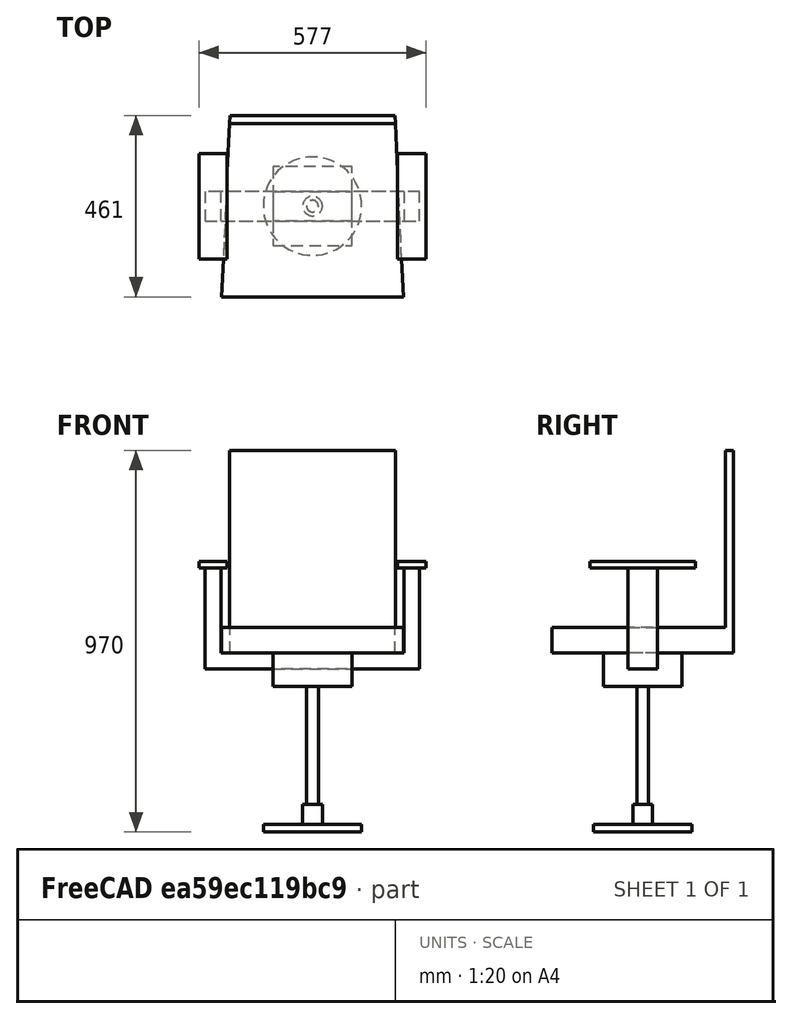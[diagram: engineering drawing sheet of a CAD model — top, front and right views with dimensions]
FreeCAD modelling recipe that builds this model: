
FCSTD DOCUMENT  (FreeCAD 1.0R39109 (Git))
Label: chair02_005
License: All rights reserved
LicenseURL: https://en.wikipedia.org/wiki/All_rights_reserved
objects: TechDraw::DrawViewDimension×26, Sketcher::SketchObject×10, PartDesign::Pad×10, TechDraw::DrawViewAnnotation×9, PartDesign::Body×5, PartDesign::ShapeBinder×4, TechDraw::DrawSVGTemplate×3, TechDraw::DrawProjGroupItem×3, TechDraw::DrawPage×3, TechDraw::DrawViewSection×3, App::Part×1
note: 108 computed .brp shape members not serialized (recipe doc carries the construction recipe); baked Part::Feature solids carry a one-line shape summary decoded from their .brp

FEATURE [Sketcher::SketchObject] Sketch
  ArcFitTolerance = 1e-06
  AttachmentSupport = -> [XY_Plane]
  FullyConstrained = true
  MakeInternals = false
  MapMode = 5
  sketch-geometry (1):
    g0: Circle CenterX=0 CenterY=0 CenterZ=0 NormalX=0 NormalY=0 NormalZ=1 AngleXU=0 Radius=125
  constraints (2):
    c: Diameter(g0) = 250
    c: Coincident(g0,g-1)
FEATURE [PartDesign::Pad] Pad
  Direction = (0,0,1)
  Length = 20
  Length2 = 10
  Profile = -> Sketch
  ReferenceAxis = -> Sketch [N_Axis]
  Refine = true
  Suppressed = false
  Type = 0
FEATURE [Sketcher::SketchObject] Sketch001
  ArcFitTolerance = 1e-06
  AttachmentSupport = -> [Pad]
  FullyConstrained = true
  MakeInternals = false
  MapMode = 5
  Placement = pos=(0,0,20) rot=(0,0,1;0rad)
  sketch-geometry (1):
    g0: Circle CenterX=0 CenterY=0 CenterZ=0 NormalX=0 NormalY=0 NormalZ=1 AngleXU=0 Radius=25
  constraints (2):
    c: Diameter(g0) = 50
    c: Coincident(g0,g-1)
FEATURE [PartDesign::Pad] Pad001
  BaseFeature = -> Pad
  Direction = (0,0,1)
  Length = 50
  Length2 = 10
  Profile = -> Sketch001
  ReferenceAxis = -> Sketch001 [N_Axis]
  Refine = true
  Suppressed = false
  Type = 0
FEATURE [PartDesign::Body] Body  label="Body1"
  AllowCompound = false
  Group = -> [Sketch,Pad,Sketch001,Pad001]
  Origin = -> Origin
  Tip = -> Pad001
FEATURE [PartDesign::ShapeBinder] CopyPad001  label="Body2_Sketch_P.lane"
  Placement = pos=(0,0,50) rot=(0,0,1;0rad)
  TraceSupport = false
FEATURE [Sketcher::SketchObject] Sketch002
  ArcFitTolerance = 1e-06
  AttachmentSupport = -> [CopyPad001]
  FullyConstrained = true
  MakeInternals = false
  MapMode = 5
  Placement = pos=(0,0,70) rot=(0,0,1;0rad)
  sketch-geometry (1):
    g0: Circle CenterX=0 CenterY=0 CenterZ=0 NormalX=0 NormalY=0 NormalZ=1 AngleXU=0 Radius=15
  constraints (2):
    c: Diameter(g0) = 30
    c: Coincident(g0,g-1)
FEATURE [PartDesign::Pad] Pad002
  Direction = (0,0,1)
  Length = 300
  Length2 = 10
  Placement = pos=(0,0,50) rot=(0,0,1;0rad)
  Profile = -> Sketch002
  ReferenceAxis = -> Sketch002 [N_Axis]
  Refine = true
  Suppressed = false
  Type = 0
FEATURE [PartDesign::Body] Body001  label="Body2"
  AllowCompound = false
  Group = -> [CopyPad001,Sketch002,Pad002]
  Origin = -> Origin001
  Tip = -> Pad002
FEATURE [PartDesign::ShapeBinder] CopyPad002  label="Body3_Sketch_Plane"
  Placement = pos=(0,0,300) rot=(0,0,1;0rad)
  TraceSupport = false
FEATURE [Sketcher::SketchObject] Sketch003
  ArcFitTolerance = 1e-06
  AttachmentSupport = -> [CopyPad002]
  FullyConstrained = true
  MakeInternals = false
  MapMode = 5
  Placement = pos=(0,0,370) rot=(0,0,1;0rad)
  sketch-geometry (5):
    g0: LineSegment StartX=-100 StartY=-100 StartZ=0 EndX=100 EndY=-100 EndZ=0
    g1: LineSegment StartX=100 StartY=-100 StartZ=0 EndX=100 EndY=100 EndZ=0
    g2: LineSegment StartX=100 StartY=100 StartZ=0 EndX=-100 EndY=100 EndZ=0
    g3: LineSegment StartX=-100 StartY=100 StartZ=0 EndX=-100 EndY=-100 EndZ=0
    g4: GeomPoint [constr] X=0 Y=0 Z=0
  constraints (12):
    c: Coincident(g0,g1)
    c: Coincident(g1,g2)
    c: Coincident(g2,g3)
    c: Coincident(g3,g0)
    c: Horizontal(g0)
    c: Horizontal(g2)
    c: Vertical(g1)
    c: Vertical(g3)
    c: Symmetric(g2,g0,g4)
    c: Distance(g1,g3) = 200
    c: Distance(g0,g2) = 200
    c: Coincident(g4,g-1)
FEATURE [PartDesign::Pad] Pad003
  Direction = (0,0,1)
  Length = 45
  Length2 = 10
  Placement = pos=(0,0,300) rot=(0,0,1;0rad)
  Profile = -> Sketch003
  ReferenceAxis = -> Sketch003 [N_Axis]
  Refine = true
  Suppressed = false
  Type = 0
FEATURE [PartDesign::ShapeBinder] CopyPad003  label="Body4_Sketch_Plane"
  Placement = pos=(0,0,45) rot=(0,0,1;0rad)
  TraceSupport = false
FEATURE [Sketcher::SketchObject] Sketch004
  ArcFitTolerance = 1e-06
  AttachmentSupport = -> [CopyPad003]
  FullyConstrained = true
  MakeInternals = false
  MapMode = 5
  Placement = pos=(0,0,415) rot=(0,0,1;0rad)
  sketch-geometry (5):
    g0: LineSegment StartX=-272.5 StartY=-37.5 StartZ=0 EndX=272.5 EndY=-37.5 EndZ=0
    g1: LineSegment StartX=272.5 StartY=-37.5 StartZ=0 EndX=272.5 EndY=37.5 EndZ=0
    g2: LineSegment StartX=272.5 StartY=37.5 StartZ=0 EndX=-272.5 EndY=37.5 EndZ=0
    g3: LineSegment StartX=-272.5 StartY=37.5 StartZ=0 EndX=-272.5 EndY=-37.5 EndZ=0
    g4: GeomPoint [constr] X=0 Y=0 Z=0
  constraints (12):
    c: Coincident(g0,g1)
    c: Coincident(g1,g2)
    c: Coincident(g2,g3)
    c: Coincident(g3,g0)
    c: Horizontal(g0)
    c: Horizontal(g2)
    c: Vertical(g1)
    c: Vertical(g3)
    c: Symmetric(g2,g0,g4)
    c: Distance(g1,g3) = 545
    c: Distance(g0,g2) = 75
    c: Coincident(g4,g-1)
FEATURE [PartDesign::Pad] Pad004
  Direction = (0,0,1)
  Length = 40
  Length2 = 10
  Placement = pos=(0,0,45) rot=(0,0,1;0rad)
  Profile = -> Sketch004
  ReferenceAxis = -> Sketch004 [N_Axis]
  Refine = true
  Suppressed = false
  Type = 0
FEATURE [Sketcher::SketchObject] Sketch005
  ArcFitTolerance = 1e-06
  AttachmentSupport = -> [Pad004]
  ExternalGeometry = -> [Pad004]
  FullyConstrained = true
  MakeInternals = false
  MapMode = 5
  Placement = pos=(0,0,455) rot=(0,0,1;0rad)
  sketch-geometry (8):
    g0: LineSegment StartX=-272.5 StartY=37.5 StartZ=0 EndX=-272.5 EndY=-37.5 EndZ=0
    g1: LineSegment StartX=-272.5 StartY=-37.5 StartZ=0 EndX=-232.5 EndY=-37.5 EndZ=0
    g2: LineSegment StartX=-232.5 StartY=-37.5 StartZ=0 EndX=-232.5 EndY=37.5 EndZ=0
    g3: LineSegment StartX=-232.5 StartY=37.5 StartZ=0 EndX=-272.5 EndY=37.5 EndZ=0
    g4: LineSegment StartX=272.5 StartY=37.5 StartZ=0 EndX=232.5 EndY=37.5 EndZ=0
    g5: LineSegment StartX=232.5 StartY=37.5 StartZ=0 EndX=232.5 EndY=-37.5 EndZ=0
    g6: LineSegment StartX=232.5 StartY=-37.5 StartZ=0 EndX=272.5 EndY=-37.5 EndZ=0
    g7: LineSegment StartX=272.5 StartY=-37.5 StartZ=0 EndX=272.5 EndY=37.5 EndZ=0
  constraints (22):
    c: Coincident(g0,g1)
    c: Coincident(g1,g2)
    c: Coincident(g2,g3)
    c: Coincident(g3,g0)
    c: Vertical(g0)
    c: Vertical(g2)
    c: Horizontal(g1)
    c: Horizontal(g3)
    c: Coincident(g0,g-3)
    c: PointOnObject(g1,g-4)
    c: DistanceX(g3,g3) = 40
    c: Coincident(g4,g5)
    c: Coincident(g5,g6)
    c: Coincident(g6,g7)
    c: Coincident(g7,g4)
    c: Horizontal(g4)
    c: Horizontal(g6)
    c: Vertical(g5)
    c: Vertical(g7)
    c: Coincident(g4,g-3)
    c: PointOnObject(g5,g-4)
    c: Equal(g4,g3)
FEATURE [PartDesign::Pad] Pad005
  BaseFeature = -> Pad004
  Direction = (0,0,1)
  Length = 216
  Length2 = 10
  Placement = pos=(0,0,45) rot=(0,0,1;0rad)
  Profile = -> Sketch005
  ReferenceAxis = -> Sketch005 [N_Axis]
  Refine = true
  Suppressed = false
  Type = 0
FEATURE [Sketcher::SketchObject] Sketch006
  ArcFitTolerance = 1e-06
  AttachmentSupport = -> [Pad005]
  ExternalGeometry = -> [Pad005]
  FullyConstrained = true
  MakeInternals = false
  MapMode = 5
  Placement = pos=(0,0,671) rot=(0,0,1;0rad)
  sketch-geometry (16):
    g0: LineSegment StartX=-288.5 StartY=134 StartZ=0 EndX=-288.5 EndY=-134 EndZ=0
    g1: LineSegment StartX=-288.5 StartY=-134 StartZ=0 EndX=-216.5 EndY=-134 EndZ=0
    g2: LineSegment StartX=-216.5 StartY=-134 StartZ=0 EndX=-216.5 EndY=134 EndZ=0
    g3: LineSegment StartX=-216.5 StartY=134 StartZ=0 EndX=-288.5 EndY=134 EndZ=0
    g4: LineSegment StartX=216.5 StartY=134 StartZ=0 EndX=216.5 EndY=-134 EndZ=0
    g5: LineSegment StartX=216.5 StartY=-134 StartZ=0 EndX=288.5 EndY=-134 EndZ=0
    g6: LineSegment StartX=288.5 StartY=-134 StartZ=0 EndX=288.5 EndY=134 EndZ=0
    g7: LineSegment StartX=288.5 StartY=134 StartZ=0 EndX=216.5 EndY=134 EndZ=0
    g8: LineSegment [constr] StartX=-272.5 StartY=37.5 StartZ=0 EndX=-232.5 EndY=-37.5 EndZ=0
    g9: LineSegment [constr] StartX=-252.5 StartY=0 StartZ=0 EndX=-272.5 EndY=-37.5 EndZ=0
    g10: LineSegment [constr] StartX=232.5 StartY=37.5 StartZ=0 EndX=272.5 EndY=-37.5 EndZ=0
    g11: LineSegment [constr] StartX=272.5 StartY=37.5 StartZ=0 EndX=252.5 EndY=0 EndZ=0
    g12: LineSegment [constr] StartX=-216.5 StartY=134 StartZ=0 EndX=-288.5 EndY=-134 EndZ=0
    g13: LineSegment [constr] StartX=-288.5 StartY=134 StartZ=0 EndX=-252.5 EndY=0 EndZ=0
    g14: LineSegment [constr] StartX=216.5 StartY=134 StartZ=0 EndX=288.5 EndY=-134 EndZ=0
    g15: LineSegment [constr] StartX=288.5 StartY=134 StartZ=0 EndX=252.5 EndY=0 EndZ=0
  constraints (38):
    c: Coincident(g0,g1)
    c: Coincident(g1,g2)
    c: Coincident(g2,g3)
    c: Coincident(g3,g0)
    c: Vertical(g0)
    c: Vertical(g2)
    c: Horizontal(g1)
    c: Horizontal(g3)
    c: Coincident(g4,g5)
    c: Coincident(g5,g6)
    c: Coincident(g6,g7)
    c: Coincident(g7,g4)
    c: Vertical(g4)
    c: Vertical(g6)
    c: Horizontal(g5)
    c: Horizontal(g7)
    c: Equal(g7,g3)
    c: Equal(g2,g4)
    c: DistanceX(g3,g3) = 72
    c: Coincident(g8,g-4)
    c: Coincident(g8,g-3)
    c: Coincident(g9,g-4)
    c: Coincident(g10,g-5)
    c: Coincident(g10,g-6)
    c: Coincident(g11,g-6)
    c: Symmetric(g10,g10,g11)
    c: Symmetric(g8,g8,g9)
    c: Coincident(g12,g2)
    c: Coincident(g12,g0)
    c: Coincident(g13,g0)
    c: Symmetric(g12,g12,g13)
    c: Coincident(g9,g13)
    c: Coincident(g14,g4)
    c: Coincident(g14,g5)
    c: Coincident(g15,g6)
    c: Symmetric(g14,g14,g15)
    c: Coincident(g15,g11)
    c: DistanceY(g2,g2) = 268
FEATURE [PartDesign::Pad] Pad006
  BaseFeature = -> Pad005
  Direction = (0,0,1)
  Length = 17
  Length2 = 10
  Placement = pos=(0,0,45) rot=(0,0,1;0rad)
  Profile = -> Sketch006
  ReferenceAxis = -> Sketch006 [N_Axis]
  Refine = true
  Suppressed = false
  Type = 0
FEATURE [PartDesign::Body] Body003  label="Body4"
  AllowCompound = false
  Group = -> [CopyPad003,Sketch004,Pad004,Sketch005,Pad005,Sketch006,Pad006]
  Origin = -> Origin003
  Tip = -> Pad006
FEATURE [PartDesign::ShapeBinder] CopyPad006  label="Body5_Sketch_Plane"
  Placement = pos=(0,0,45) rot=(0,0,1;0rad)
  TraceSupport = false
FEATURE [Sketcher::SketchObject] Sketch009
  ArcFitTolerance = 1e-06
  AttachmentSupport = -> [Pad003]
  ExternalGeometry = -> [Pad003]
  FullyConstrained = true
  MakeInternals = false
  MapMode = 5
  Placement = pos=(0,0,415) rot=(0,0,1;0rad)
  sketch-geometry (8):
    g0: LineSegment StartX=-100 StartY=100 StartZ=0 EndX=-100 EndY=37.5 EndZ=0
    g1: LineSegment StartX=-100 StartY=37.5 StartZ=0 EndX=100 EndY=37.5 EndZ=0
    g2: LineSegment StartX=100 StartY=37.5 StartZ=0 EndX=100 EndY=100 EndZ=0
    g3: LineSegment StartX=100 StartY=100 StartZ=0 EndX=-100 EndY=100 EndZ=0
    g4: LineSegment StartX=100 StartY=-100 StartZ=0 EndX=100 EndY=-37.5 EndZ=0
    g5: LineSegment StartX=100 StartY=-37.5 StartZ=0 EndX=-100 EndY=-37.5 EndZ=0
    g6: LineSegment StartX=-100 StartY=-37.5 StartZ=0 EndX=-100 EndY=-100 EndZ=0
    g7: LineSegment StartX=-100 StartY=-100 StartZ=0 EndX=100 EndY=-100 EndZ=0
  constraints (21):
    c: Coincident(g0,g1)
    c: Coincident(g1,g2)
    c: Coincident(g2,g3)
    c: Coincident(g3,g0)
    c: Vertical(g0)
    c: Vertical(g2)
    c: Horizontal(g1)
    c: Horizontal(g3)
    c: Coincident(g0,g-3)
    c: PointOnObject(g1,g-4)
    c: Coincident(g4,g5)
    c: Coincident(g5,g6)
    c: Coincident(g6,g7)
    c: Coincident(g7,g4)
    c: Vertical(g6)
    c: Horizontal(g5)
    c: Horizontal(g7)
    c: Coincident(g4,g-4)
    c: PointOnObject(g5,g-3)
    c: DistanceY(g4,g1) = 75
    c: Symmetric(g1,g4,g-1)
FEATURE [PartDesign::Pad] Pad009
  BaseFeature = -> Pad003
  Direction = (0,0,1)
  Length = 40
  Length2 = 10
  Placement = pos=(0,0,300) rot=(0,0,1;0rad)
  Profile = -> Sketch009
  ReferenceAxis = -> Sketch009 [N_Axis]
  Refine = true
  Suppressed = false
  Type = 0
FEATURE [PartDesign::Body] Body002  label="Body3"
  AllowCompound = false
  Group = -> [CopyPad002,Sketch003,Pad003,Sketch009,Pad009]
  Origin = -> Origin002
  Tip = -> Pad009
FEATURE [Sketcher::SketchObject] Sketch007
  ArcFitTolerance = 1e-06
  AttachmentSupport = -> [CopyPad006]
  FullyConstrained = true
  MakeInternals = false
  MapMode = 5
  Placement = pos=(0,0,455) rot=(0,0,1;0rad)
  sketch-geometry (8):
    g0: LineSegment StartX=-210 StartY=230.5 StartZ=0 EndX=-231 EndY=-230.5 EndZ=0
    g1: LineSegment StartX=-231 StartY=-230.5 StartZ=0 EndX=231 EndY=-230.5 EndZ=0
    g2: LineSegment StartX=231 StartY=-230.5 StartZ=0 EndX=210 EndY=230.5 EndZ=0
    g3: LineSegment StartX=210 StartY=230.5 StartZ=0 EndX=-210 EndY=230.5 EndZ=0
    g4: LineSegment [constr] StartX=210 StartY=230.5 StartZ=0 EndX=2.84e-14 EndY=0 EndZ=0
    g5: LineSegment [constr] StartX=2.84e-14 StartY=0 StartZ=0 EndX=-210 EndY=230.5 EndZ=0
    g6: LineSegment [constr] StartX=210 StartY=230.5 StartZ=0 EndX=210 EndY=0 EndZ=0
    g7: LineSegment [constr] StartX=231 StartY=-230.5 StartZ=0 EndX=231 EndY=0 EndZ=0
  constraints (20):
    c: Coincident(g2,g1)
    c: DistanceX(g1,g1) = 462
    c: DistanceX(g3,g3) = 420
    c: Coincident(g1,g0)
    c: Symmetric(g2,g0,g-2)
    c: Coincident(g2,g3)
    c: Coincident(g3,g0)
    c: Coincident(g4,g2)
    c: Coincident(g4,g-1)
    c: Coincident(g5,g4)
    c: Coincident(g5,g0)
    c: DistanceY(g2,g2) = 461
    c: Coincident(g6,g2)
    c: PointOnObject(g6,g-1)
    c: Vertical(g6)
    c: Coincident(g7,g1)
    c: PointOnObject(g7,g-1)
    c: Vertical(g7)
    c: Equal(g7,g6)
    c: Symmetric(g1,g0,g-2)
FEATURE [PartDesign::Pad] Pad007
  Direction = (0,0,1)
  Length = 65
  Length2 = 10
  Placement = pos=(0,0,45) rot=(0,0,1;0rad)
  Profile = -> Sketch007
  ReferenceAxis = -> Sketch007 [N_Axis]
  Refine = true
  Suppressed = false
  Type = 0
FEATURE [Sketcher::SketchObject] Sketch008
  ArcFitTolerance = 1e-06
  AttachmentSupport = -> [Pad007]
  ExternalGeometry = -> [Pad007]
  FullyConstrained = true
  MakeInternals = false
  MapMode = 5
  Placement = pos=(0,0,520) rot=(0,0,1;0rad)
  sketch-geometry (4):
    g0: LineSegment StartX=-210 StartY=230.5 StartZ=0 EndX=210 EndY=230.5 EndZ=0
    g1: LineSegment StartX=-210 StartY=230.5 StartZ=0 EndX=-210.957 EndY=209.5 EndZ=0
    g2: LineSegment StartX=-210.957 StartY=209.5 StartZ=0 EndX=210.957 EndY=209.5 EndZ=0
    g3: LineSegment StartX=210 StartY=230.5 StartZ=0 EndX=210.957 EndY=209.5 EndZ=0
  constraints (10):
    c: Coincident(g0,g-3)
    c: Coincident(g0,g-4)
    c: Coincident(g1,g0)
    c: PointOnObject(g1,g-3)
    c: Coincident(g2,g1)
    c: PointOnObject(g2,g-4)
    c: Horizontal(g2)
    c: Coincident(g3,g0)
    c: Coincident(g3,g2)
    c: DistanceY(g1,g1) = 21
FEATURE [PartDesign::Pad] Pad008
  BaseFeature = -> Pad007
  Direction = (0,0,1)
  Length = 450
  Length2 = 10
  Placement = pos=(0,0,45) rot=(0,0,1;0rad)
  Profile = -> Sketch008
  ReferenceAxis = -> Sketch008 [N_Axis]
  Refine = true
  Suppressed = false
  Type = 0
FEATURE [PartDesign::Body] Body004  label="Body5"
  AllowCompound = false
  Group = -> [CopyPad006,Sketch007,Pad007,Sketch008,Pad008]
  Origin = -> Origin004
  Tip = -> Pad008
FEATURE [App::Part] Part  label="chair02"
  Group = -> [Body,Body001,Body002,Body003,Body004]
  Origin = -> Origin005
FEATURE [TechDraw::DrawSVGTemplate] Template  label="テンプレート"
  Height = 210
  Orientation = 1
  Template = <userpath>/AppData/Local/Programs/FreeCAD 1.0/data/Mod/TechDraw/Templates/A4_Landscape_blank.svg
  Width = 297
FEATURE [TechDraw::DrawProjGroupItem] View
  CoarseView = false
  Direction = (0,0,1)
  Focus = 100
  HardHidden = true
  IsoCount = 0
  IsoHidden = false
  IsoVisible = false
  LockPosition = false
  Perspective = false
  Rotation = 0
  RotationVector = (1,0,0)
  Scale = 0.333333
  ScaleType = 2
  ScrubCount = 1
  SeamHidden = false
  SeamVisible = false
  SmoothHidden = false
  SmoothVisible = true
  Source = -> [Part]
  Type = 0
  X = 131.425
  XDirection = (1,0,0)
  Y = 107.897
FEATURE [TechDraw::DrawViewDimension] Dimension  label="寸法"
  AngleOverride = false
  Arbitrary = false
  ArbitraryTolerances = false
  BoxCorners = (2) [(-96.1666,-76.8333,0),(96.1666,76.8333,0)]
  EqualTolerance = true
  ExtensionAngle = 0
  FormatSpec = %.2w
  FormatSpecOverTolerance = %+.2w
  FormatSpecUnderTolerance = %+.2w
  Inverted = false
  LineAngle = 0
  LockPosition = false
  MeasureType = 1
  OverTolerance = 0
  References2D = -> [View]
  Rotation = 0
  Scale = 0.2
  ScaleType = 2
  TheoreticalExact = false
  Type = 1
  UnderTolerance = 0
  X = 0
  Y = 93.9298
FEATURE [TechDraw::DrawViewDimension] Dimension001  label="寸法001"
  AngleOverride = false
  Arbitrary = false
  ArbitraryTolerances = false
  BoxCorners = (2) [(-96.1666,-76.8333,0),(96.1666,76.8333,0)]
  EqualTolerance = true
  ExtensionAngle = 0
  FormatSpec = %.2w
  FormatSpecOverTolerance = %+.2w
  FormatSpecUnderTolerance = %+.2w
  Inverted = false
  LineAngle = 0
  LockPosition = false
  MeasureType = 1
  OverTolerance = 0
  References2D = -> [View]
  Rotation = 0
  Scale = 0.2
  ScaleType = 2
  TheoreticalExact = false
  Type = 2
  UnderTolerance = 0
  X = 135.701
  Y = 0
FEATURE [TechDraw::DrawViewDimension] Dimension002  label="寸法002"
  AngleOverride = false
  Arbitrary = false
  ArbitraryTolerances = false
  BoxCorners = (2) [(-96.1666,-76.8333,0),(96.1666,76.8333,0)]
  EqualTolerance = true
  ExtensionAngle = 0
  FormatSpec = %.2w
  FormatSpecOverTolerance = %+.2w
  FormatSpecUnderTolerance = %+.2w
  Inverted = false
  LineAngle = 0
  LockPosition = false
  MeasureType = 1
  OverTolerance = 0
  References2D = -> [View]
  Rotation = 0
  Scale = 0.2
  ScaleType = 2
  TheoreticalExact = false
  Type = 2
  UnderTolerance = 0
  X = 113.57
  Y = 61.6706
FEATURE [TechDraw::DrawViewDimension] Dimension003  label="寸法003"
  AngleOverride = false
  Arbitrary = false
  ArbitraryTolerances = false
  BoxCorners = (2) [(-96.1666,-76.8333,0),(96.1666,76.8333,0)]
  EqualTolerance = true
  ExtensionAngle = 0
  FormatSpec = %.2w
  FormatSpecOverTolerance = %+.2w
  FormatSpecUnderTolerance = %+.2w
  Inverted = false
  LineAngle = 0
  LockPosition = false
  MeasureType = 1
  OverTolerance = 0
  References2D = -> [View]
  Rotation = 0
  Scale = 0.2
  ScaleType = 2
  TheoreticalExact = false
  Type = 2
  UnderTolerance = 0
  X = 125.233
  Y = 0.063601
FEATURE [TechDraw::DrawViewDimension] Dimension004  label="寸法004"
  AngleOverride = false
  Arbitrary = false
  ArbitraryTolerances = false
  BoxCorners = (2) [(-96.1666,-76.8333,0),(96.1666,76.8333,0)]
  EqualTolerance = true
  ExtensionAngle = 0
  FormatSpec = %.2w
  FormatSpecOverTolerance = %+.2w
  FormatSpecUnderTolerance = %+.2w
  Inverted = false
  LineAngle = 0
  LockPosition = false
  MeasureType = 1
  OverTolerance = 0
  References2D = -> [View]
  Rotation = 0
  Scale = 0.2
  ScaleType = 2
  TheoreticalExact = false
  Type = 1
  UnderTolerance = 0
  X = -84.1666
  Y = 58.5053
FEATURE [TechDraw::DrawViewDimension] Dimension005  label="寸法005"
  AngleOverride = false
  Arbitrary = false
  ArbitraryTolerances = false
  BoxCorners = (2) [(-96.1666,-76.8333,0),(96.1666,76.8333,0)]
  EqualTolerance = true
  ExtensionAngle = 0
  FormatSpec = %.2w
  FormatSpecOverTolerance = %+.2w
  FormatSpecUnderTolerance = %+.2w
  Inverted = false
  LineAngle = 0
  LockPosition = false
  MeasureType = 1
  OverTolerance = 0
  References2D = -> [View]
  Rotation = 0
  Scale = 0.2
  ScaleType = 2
  TheoreticalExact = false
  Type = 2
  UnderTolerance = 0
  X = -108.801
  Y = 0
FEATURE [TechDraw::DrawViewDimension] Dimension006  label="寸法006"
  AngleOverride = false
  Arbitrary = false
  ArbitraryTolerances = false
  BoxCorners = (2) [(-96.1666,-76.8333,0),(96.1666,76.8333,0)]
  EqualTolerance = true
  ExtensionAngle = 0
  FormatSpec = %.2w
  FormatSpecOverTolerance = %+.2w
  FormatSpecUnderTolerance = %+.2w
  Inverted = false
  LineAngle = 0
  LockPosition = false
  MeasureType = 1
  OverTolerance = 0
  References2D = -> [View]
  Rotation = 0
  Scale = 0.2
  ScaleType = 2
  TheoreticalExact = false
  Type = 1
  UnderTolerance = 0
  X = 0
  Y = -83.8244
FEATURE [TechDraw::DrawPage] Page  label="用紙"
  KeepUpdated = true
  NextBalloonIndex = 1
  ProjectionType = 0
  Template = -> Template
  Views = -> [View,Dimension,Dimension001,Dimension002,Dimension003,Dimension004,Dimension005,Dimension006]
FEATURE [TechDraw::DrawSVGTemplate] Template001  label="テンプレート001"
  Height = 210
  Orientation = 1
  Template = <userpath>/AppData/Local/Programs/FreeCAD 1.0/data/Mod/TechDraw/Templates/A4_Landscape_blank.svg
  Width = 297
FEATURE [TechDraw::DrawSVGTemplate] Template002  label="テンプレート002"
  Height = 210
  Orientation = 1
  Template = <userpath>/AppData/Local/Programs/FreeCAD 1.0/data/Mod/TechDraw/Templates/A4_Landscape_blank.svg
  Width = 297
FEATURE [TechDraw::DrawProjGroupItem] View001
  CoarseView = false
  Direction = (0,-1,0)
  Focus = 100
  HardHidden = true
  IsoCount = 0
  IsoHidden = false
  IsoVisible = false
  LockPosition = false
  Perspective = false
  Rotation = 0
  RotationVector = (1,0,0)
  Scale = 0.2
  ScaleType = 2
  ScrubCount = 1
  SeamHidden = false
  SeamVisible = false
  SmoothHidden = false
  SmoothVisible = true
  Source = -> [Part]
  Type = 0
  X = 72.2264
  XDirection = (1,0,0)
  Y = 108.632
FEATURE [TechDraw::DrawViewSection] SectionView  label="セクション  - "
  BaseView = -> View001
  CoarseView = false
  CutSurfaceDisplay = 2
  Direction = (1e-16,0,1)
  FileGeomPattern = <userpath>\AppData\Local\Programs\FreeCAD 1.0\data\Mod/TechDraw/PAT/FCPAT.pat
  FileHatchPattern = <userpath>\AppData\Local\Programs\FreeCAD 1.0\data\Mod/TechDraw/Patterns/simple.svg
  Focus = 100
  FuseBeforeCut = false
  HardHidden = true
  HatchOffset = (0,0,0)
  HatchRotation = 0
  HatchScale = 1
  IsoCount = 0
  IsoHidden = false
  IsoVisible = false
  LockPosition = false
  NameGeomPattern = Diamond
  Perspective = false
  Rotation = 0
  Scale = 0.15
  ScaleType = 2
  ScrubCount = 1
  SeamHidden = false
  SeamVisible = false
  SectionDirection = 4
  SectionLineStretch = 1
  SectionNormal = (1e-16,0,1)
  SectionOrigin = (0,0,581)
  SmoothHidden = false
  SmoothVisible = true
  Source = -> [Part]
  TrimAfterCut = false
  UsePreviousCut = false
  X = 215.858
  XDirection = (1,0,-1e-16)
  Y = 166.085
FEATURE [TechDraw::DrawViewSection] SectionView001  label="セクション001  - "
  BaseView = -> View001
  CoarseView = false
  CutSurfaceDisplay = 2
  Direction = (1e-16,0,1)
  FileGeomPattern = <userpath>\AppData\Local\Programs\FreeCAD 1.0\data\Mod/TechDraw/PAT/FCPAT.pat
  FileHatchPattern = <userpath>\AppData\Local\Programs\FreeCAD 1.0\data\Mod/TechDraw/Patterns/simple.svg
  Focus = 100
  FuseBeforeCut = false
  HardHidden = true
  HatchOffset = (0,0,0)
  HatchRotation = 0
  HatchScale = 1
  IsoCount = 0
  IsoHidden = false
  IsoVisible = false
  LockPosition = false
  NameGeomPattern = Diamond
  Perspective = false
  Rotation = 0
  Scale = 0.15
  ScaleType = 2
  ScrubCount = 1
  SeamHidden = false
  SeamVisible = false
  SectionDirection = 4
  SectionLineStretch = 1
  SectionNormal = (1e-16,0,1)
  SectionOrigin = (0,0,437)
  SmoothHidden = false
  SmoothVisible = true
  Source = -> [Part]
  TrimAfterCut = false
  UsePreviousCut = false
  X = 215.086
  XDirection = (1,0,-1e-16)
  Y = 92.3168
FEATURE [TechDraw::DrawViewSection] SectionView002  label="セクション002  - "
  BaseView = -> View001
  CoarseView = false
  CutSurfaceDisplay = 2
  Direction = (1e-16,0,1)
  FileGeomPattern = <userpath>\AppData\Local\Programs\FreeCAD 1.0\data\Mod/TechDraw/PAT/FCPAT.pat
  FileHatchPattern = <userpath>\AppData\Local\Programs\FreeCAD 1.0\data\Mod/TechDraw/Patterns/simple.svg
  Focus = 100
  FuseBeforeCut = false
  HardHidden = true
  HatchOffset = (0,0,0)
  HatchRotation = 0
  HatchScale = 1
  IsoCount = 0
  IsoHidden = false
  IsoVisible = false
  LockPosition = false
  NameGeomPattern = Diamond
  Perspective = false
  Rotation = 0
  Scale = 0.15
  ScaleType = 2
  ScrubCount = 1
  SeamHidden = false
  SeamVisible = false
  SectionDirection = 4
  SectionLineStretch = 1
  SectionNormal = (1e-16,0,1)
  SectionOrigin = (0,0,200)
  SmoothHidden = false
  SmoothVisible = true
  Source = -> [Part]
  TrimAfterCut = false
  UsePreviousCut = false
  X = 214.868
  XDirection = (1,0,-1e-16)
  Y = 24.434
FEATURE [TechDraw::DrawViewDimension] Dimension007  label="寸法007"
  AngleOverride = false
  Arbitrary = false
  ArbitraryTolerances = false
  BoxCorners = (2) [(-40.875,-34.575,0),(40.875,34.575,0)]
  EqualTolerance = true
  ExtensionAngle = 0
  FormatSpec = %.2w
  FormatSpecOverTolerance = %+.2w
  FormatSpecUnderTolerance = %+.2w
  Inverted = false
  LineAngle = 0
  LockPosition = false
  MeasureType = 1
  OverTolerance = 0
  References2D = -> [SectionView]
  Rotation = 0
  Scale = 0.2
  ScaleType = 2
  TheoreticalExact = false
  Type = 1
  UnderTolerance = 0
  X = 48.3858
  Y = 24.3952
FEATURE [TechDraw::DrawViewDimension] Dimension008  label="寸法008"
  AngleOverride = false
  Arbitrary = false
  ArbitraryTolerances = false
  BoxCorners = (2) [(-40.875,-34.575,0),(40.875,34.575,0)]
  EqualTolerance = true
  ExtensionAngle = 0
  FormatSpec = %.2w
  FormatSpecOverTolerance = %+.2w
  FormatSpecUnderTolerance = %+.2w
  Inverted = false
  LineAngle = 0
  LockPosition = false
  MeasureType = 1
  OverTolerance = 0
  References2D = -> [SectionView]
  Rotation = 0
  Scale = 0.2
  ScaleType = 2
  TheoreticalExact = false
  Type = 2
  UnderTolerance = 0
  X = 59.3049
  Y = -11.5187
FEATURE [TechDraw::DrawViewDimension] Dimension009  label="寸法009"
  AngleOverride = false
  Arbitrary = false
  ArbitraryTolerances = false
  BoxCorners = (2) [(-40.875,-18.75,0),(40.875,18.75,0)]
  EqualTolerance = true
  ExtensionAngle = 0
  FormatSpec = %.2w
  FormatSpecOverTolerance = %+.2w
  FormatSpecUnderTolerance = %+.2w
  Inverted = false
  LineAngle = 0
  LockPosition = false
  MeasureType = 1
  OverTolerance = 0
  References2D = -> [SectionView001]
  Rotation = 0
  Scale = 0.2
  ScaleType = 2
  TheoreticalExact = false
  Type = 1
  UnderTolerance = 0
  X = 0
  Y = -24.3529
FEATURE [TechDraw::DrawViewDimension] Dimension010  label="寸法010"
  AngleOverride = false
  Arbitrary = false
  ArbitraryTolerances = false
  BoxCorners = (2) [(-40.875,-18.75,0),(40.875,18.75,0)]
  EqualTolerance = true
  ExtensionAngle = 0
  FormatSpec = %.2w
  FormatSpecOverTolerance = %+.2w
  FormatSpecUnderTolerance = %+.2w
  Inverted = false
  LineAngle = 0
  LockPosition = false
  MeasureType = 1
  OverTolerance = 0
  References2D = -> [SectionView001]
  Rotation = 0
  Scale = 0.2
  ScaleType = 2
  TheoreticalExact = false
  Type = 1
  UnderTolerance = 0
  X = -23.2227
  Y = -15.8558
FEATURE [TechDraw::DrawViewDimension] Dimension011  label="寸法011"
  AngleOverride = false
  Arbitrary = false
  ArbitraryTolerances = false
  BoxCorners = (2) [(-40.875,-18.75,0),(40.875,18.75,0)]
  EqualTolerance = true
  ExtensionAngle = 0
  FormatSpec = %.2w
  FormatSpecOverTolerance = %+.2w
  FormatSpecUnderTolerance = %+.2w
  Inverted = false
  LineAngle = 0
  LockPosition = false
  MeasureType = 1
  OverTolerance = 0
  References2D = -> [SectionView001]
  Rotation = 0
  Scale = 0.2
  ScaleType = 2
  TheoreticalExact = false
  Type = 2
  UnderTolerance = 0
  X = 58.5124
  Y = 0
FEATURE [TechDraw::DrawViewDimension] Dimension012  label="寸法012"
  AngleOverride = false
  Arbitrary = false
  ArbitraryTolerances = false
  BoxCorners = (2) [(-40.875,-18.75,0),(40.875,18.75,0)]
  EqualTolerance = true
  ExtensionAngle = 0
  FormatSpec = %.2w
  FormatSpecOverTolerance = %+.2w
  FormatSpecUnderTolerance = %+.2w
  Inverted = false
  LineAngle = 0
  LockPosition = false
  MeasureType = 1
  OverTolerance = 0
  References2D = -> [SectionView001]
  Rotation = 0
  Scale = 0.2
  ScaleType = 2
  TheoreticalExact = false
  Type = 2
  UnderTolerance = 0
  X = 72.3404
  Y = 0
FEATURE [TechDraw::DrawViewDimension] Dimension013  label="寸法013"
  AngleOverride = false
  Arbitrary = false
  ArbitraryTolerances = false
  BoxCorners = (2) [(-18.75,-18.75,0),(18.75,18.75,0)]
  EqualTolerance = true
  ExtensionAngle = 0
  FormatSpec = ⌀%.2w
  FormatSpecOverTolerance = %+.2w
  FormatSpecUnderTolerance = %+.2w
  Inverted = false
  LineAngle = 0
  LockPosition = false
  MeasureType = 1
  OverTolerance = 0
  References2D = -> [SectionView002]
  Rotation = 0
  Scale = 0.2
  ScaleType = 2
  TheoreticalExact = false
  Type = 5
  UnderTolerance = 0
  X = 8.10016
  Y = -8.95927
FEATURE [TechDraw::DrawViewDimension] Dimension014  label="寸法014"
  AngleOverride = false
  Arbitrary = false
  ArbitraryTolerances = false
  BoxCorners = (2) [(-18.75,-18.75,0),(18.75,18.75,0)]
  EqualTolerance = true
  ExtensionAngle = 0
  FormatSpec = ⌀%.2w
  FormatSpecOverTolerance = %+.2w
  FormatSpecUnderTolerance = %+.2w
  Inverted = false
  LineAngle = 0
  LockPosition = false
  MeasureType = 1
  OverTolerance = 0
  References2D = -> [SectionView002]
  Rotation = 0
  Scale = 0.2
  ScaleType = 2
  TheoreticalExact = false
  Type = 5
  UnderTolerance = 0
  X = 10.9229
  Y = 0.736379
FEATURE [TechDraw::DrawViewDimension] Dimension015  label="寸法015"
  AngleOverride = false
  Arbitrary = false
  ArbitraryTolerances = false
  BoxCorners = (2) [(-18.75,-18.75,0),(18.75,18.75,0)]
  EqualTolerance = true
  ExtensionAngle = 0
  FormatSpec = ⌀%.2w
  FormatSpecOverTolerance = %+.2w
  FormatSpecUnderTolerance = %+.2w
  Inverted = false
  LineAngle = 0
  LockPosition = false
  MeasureType = 1
  OverTolerance = 0
  References2D = -> [SectionView002]
  Rotation = 0
  Scale = 0.2
  ScaleType = 2
  TheoreticalExact = false
  Type = 5
  UnderTolerance = 0
  X = 22.705
  Y = 18.6549
FEATURE [TechDraw::DrawViewDimension] Dimension016  label="寸法016"
  AngleOverride = false
  Arbitrary = false
  ArbitraryTolerances = false
  BoxCorners = (2) [(-40.875,-34.575,0),(40.875,34.575,0)]
  EqualTolerance = true
  ExtensionAngle = 0
  FormatSpec = %.2w
  FormatSpecOverTolerance = %+.2w
  FormatSpecUnderTolerance = %+.2w
  Inverted = false
  LineAngle = 0
  LockPosition = false
  MeasureType = 1
  OverTolerance = 0
  References2D = -> [SectionView]
  Rotation = 0
  Scale = 0.2
  ScaleType = 2
  TheoreticalExact = false
  Type = 1
  UnderTolerance = 0
  X = 21.6748
  Y = -21.6209
FEATURE [TechDraw::DrawViewAnnotation] Annotation  label="注釈"
  Font = osifont
  LineSpace = 100
  LockPosition = false
  MaxWidth = -1
  Rotation = 0
  Scale = 0.2
  ScaleType = 2
  Text = A
  TextSize = 5
  TextStyle = 0
  X = 143.937
  Y = 118.99
FEATURE [TechDraw::DrawViewAnnotation] Annotation001  label="注釈001"
  Font = osifont
  LineSpace = 100
  LockPosition = false
  MaxWidth = -1
  Rotation = 0
  Scale = 0.2
  ScaleType = 2
  Text = A
  TextSize = 5
  TextStyle = 0
  X = 9.25009
  Y = 118.99
FEATURE [TechDraw::DrawViewAnnotation] Annotation002  label="注釈002"
  Font = osifont
  LineSpace = 100
  LockPosition = false
  MaxWidth = -1
  Rotation = 0
  Scale = 0.2
  ScaleType = 2
  Text = B
  TextSize = 5
  TextStyle = 0
  X = 9.25009
  Y = 89.4351
FEATURE [TechDraw::DrawViewAnnotation] Annotation003  label="注釈003"
  Font = osifont
  LineSpace = 100
  LockPosition = false
  MaxWidth = -1
  Rotation = 0
  Scale = 0.2
  ScaleType = 2
  Text = B
  TextSize = 5
  TextStyle = 0
  X = 145.458
  Y = 89.4351
FEATURE [TechDraw::DrawViewAnnotation] Annotation004  label="注釈004"
  Font = osifont
  LineSpace = 100
  LockPosition = false
  MaxWidth = -1
  Rotation = 0
  Scale = 0.2
  ScaleType = 2
  Text = C
  TextSize = 5
  TextStyle = 0
  X = 145.458
  Y = 40.7495
FEATURE [TechDraw::DrawViewAnnotation] Annotation005  label="注釈005"
  Font = osifont
  LineSpace = 100
  LockPosition = false
  MaxWidth = -1
  Rotation = 0
  Scale = 0.2
  ScaleType = 2
  Text = C
  TextSize = 5
  TextStyle = 0
  X = 9.25009
  Y = 43.6474
FEATURE [TechDraw::DrawViewAnnotation] Annotation006  label="注釈006"
  Font = osifont
  LineSpace = 100
  LockPosition = false
  MaxWidth = -1
  Rotation = 0
  Scale = 0.2
  ScaleType = 2
  Text = A-A
  TextSize = 5
  TextStyle = 0
  X = 215.858
  Y = 205.891
FEATURE [TechDraw::DrawViewAnnotation] Annotation007  label="注釈007"
  Font = osifont
  LineSpace = 100
  LockPosition = false
  MaxWidth = -1
  Rotation = 0
  Scale = 0.2
  ScaleType = 2
  Text = B-B
  TextSize = 5
  TextStyle = 0
  X = 215.858
  Y = 117.871
FEATURE [TechDraw::DrawViewAnnotation] Annotation008  label="注釈008"
  Font = osifont
  LineSpace = 100
  LockPosition = false
  MaxWidth = -1
  Rotation = 0
  Scale = 0.2
  ScaleType = 2
  Text = C -C
  TextSize = 5
  TextStyle = 0
  X = 215.858
  Y = 48.4539
FEATURE [TechDraw::DrawPage] Page002  label="用紙002"
  KeepUpdated = true
  NextBalloonIndex = 1
  ProjectionType = 0
  Template = -> Template002
  Views = -> [View001,SectionView,SectionView001,SectionView002,Dimension007,Dimension008,Dimension009,Dimension010,Dimension011,Dimension012,Dimension013,Dimension014,Dimension015,Dimension016,Annotation,Annotation001,Annotation002,Annotation003,Annotation004,Annotation005,Annotation006,Annotation007,Annotation008]
FEATURE [TechDraw::DrawProjGroupItem] View002
  CoarseView = false
  Direction = (0,-1,0)
  Focus = 100
  HardHidden = true
  IsoCount = 0
  IsoHidden = false
  IsoVisible = false
  LockPosition = false
  Perspective = false
  Rotation = 0
  RotationVector = (1,0,0)
  Scale = 0.2
  ScaleType = 2
  ScrubCount = 1
  SeamHidden = false
  SeamVisible = false
  SmoothHidden = false
  SmoothVisible = true
  Source = -> [Part]
  Type = 0
  X = 144.274
  XDirection = (1,0,0)
  Y = 104.736
FEATURE [TechDraw::DrawViewDimension] Dimension017  label="寸法017"
  AngleOverride = false
  Arbitrary = false
  ArbitraryTolerances = false
  BoxCorners = (2) [(-48.0834,-80.8335,-1e-07),(48.0834,80.8335,1e-07)]
  EqualTolerance = true
  ExtensionAngle = 0
  FormatSpec = %.2w
  FormatSpecOverTolerance = %+.2w
  FormatSpecUnderTolerance = %+.2w
  Inverted = false
  LineAngle = 0
  LockPosition = false
  MeasureType = 1
  OverTolerance = 0
  References2D = -> [View002]
  Rotation = 0
  Scale = 0.2
  ScaleType = 2
  TheoreticalExact = false
  Type = 2
  UnderTolerance = 0
  X = 71.6242
  Y = 43.3334
FEATURE [TechDraw::DrawViewDimension] Dimension019  label="寸法019"
  AngleOverride = false
  Arbitrary = false
  ArbitraryTolerances = false
  BoxCorners = (2) [(-48.0834,-80.8335,-1e-07),(48.0834,80.8335,1e-07)]
  EqualTolerance = true
  ExtensionAngle = 0
  FormatSpec = %.2w
  FormatSpecOverTolerance = %+.2w
  FormatSpecUnderTolerance = %+.2w
  Inverted = false
  LineAngle = 0
  LockPosition = false
  MeasureType = 1
  OverTolerance = 0
  References2D = -> [View002]
  Rotation = 0
  Scale = 0.2
  ScaleType = 2
  TheoreticalExact = false
  Type = 2
  UnderTolerance = 0
  X = 71.6242
  Y = 0.416668
FEATURE [TechDraw::DrawViewDimension] Dimension021  label="寸法021"
  AngleOverride = false
  Arbitrary = false
  ArbitraryTolerances = false
  BoxCorners = (2) [(-48.0834,-80.8335,-1e-07),(48.0834,80.8335,1e-07)]
  EqualTolerance = true
  ExtensionAngle = 0
  FormatSpec = %.2w
  FormatSpecOverTolerance = %+.2w
  FormatSpecUnderTolerance = %+.2w
  Inverted = false
  LineAngle = 0
  LockPosition = false
  MeasureType = 1
  OverTolerance = 0
  References2D = -> [View002]
  Rotation = 0
  Scale = 0.2
  ScaleType = 2
  TheoreticalExact = false
  Type = 2
  UnderTolerance = 0
  X = 64.6242
  Y = -30.3933
FEATURE [TechDraw::DrawViewDimension] Dimension022  label="寸法022"
  AngleOverride = false
  Arbitrary = false
  ArbitraryTolerances = false
  BoxCorners = (2) [(-48.0834,-80.8335,-1e-07),(48.0834,80.8335,1e-07)]
  EqualTolerance = true
  ExtensionAngle = 0
  FormatSpec = %.2w
  FormatSpecOverTolerance = %+.2w
  FormatSpecUnderTolerance = %+.2w
  Inverted = false
  LineAngle = 0
  LockPosition = false
  MeasureType = 1
  OverTolerance = 0
  References2D = -> [View002]
  Rotation = 0
  Scale = 0.2
  ScaleType = 2
  TheoreticalExact = false
  Type = 2
  UnderTolerance = 0
  X = 44.6521
  Y = -44.1668
FEATURE [TechDraw::DrawViewDimension] Dimension025  label="寸法025"
  AngleOverride = false
  Arbitrary = false
  ArbitraryTolerances = false
  BoxCorners = (2) [(-48.0834,-80.8335,-1e-07),(48.0834,80.8335,1e-07)]
  EqualTolerance = true
  ExtensionAngle = 0
  FormatSpec = %.2w
  FormatSpecOverTolerance = %+.2w
  FormatSpecUnderTolerance = %+.2w
  Inverted = false
  LineAngle = 0
  LockPosition = false
  MeasureType = 1
  OverTolerance = 0
  References2D = -> [View002]
  Rotation = 0
  Scale = 0.2
  ScaleType = 2
  TheoreticalExact = false
  Type = 0
  UnderTolerance = 0
  X = 44.6521
  Y = -73.3335
FEATURE [TechDraw::DrawViewDimension] Dimension026  label="寸法026"
  AngleOverride = false
  Arbitrary = false
  ArbitraryTolerances = false
  BoxCorners = (2) [(-48.0834,-80.8335,-1e-07),(48.0834,80.8335,1e-07)]
  EqualTolerance = true
  ExtensionAngle = 0
  FormatSpec = %.2w
  FormatSpecOverTolerance = %+.2w
  FormatSpecUnderTolerance = %+.2w
  Inverted = false
  LineAngle = 0
  LockPosition = false
  MeasureType = 1
  OverTolerance = 0
  References2D = -> [View002]
  Rotation = 0
  Scale = 0.2
  ScaleType = 2
  TheoreticalExact = false
  Type = 0
  UnderTolerance = 0
  X = 30.6063
  Y = -88.96
FEATURE [TechDraw::DrawViewDimension] Dimension027  label="寸法027"
  AngleOverride = false
  Arbitrary = false
  ArbitraryTolerances = false
  BoxCorners = (2) [(-48.0834,-80.8335,-1e-07),(48.0834,80.8335,1e-07)]
  EqualTolerance = true
  ExtensionAngle = 0
  FormatSpec = %.2w
  FormatSpecOverTolerance = %+.2w
  FormatSpecUnderTolerance = %+.2w
  Inverted = false
  LineAngle = 0
  LockPosition = false
  MeasureType = 1
  OverTolerance = 0
  References2D = -> [View002]
  Rotation = 0
  Scale = 0.2
  ScaleType = 2
  TheoreticalExact = false
  Type = 2
  UnderTolerance = 0
  X = -107.03
  Y = 11.6
FEATURE [TechDraw::DrawViewDimension] Dimension028  label="寸法028"
  AngleOverride = false
  Arbitrary = false
  ArbitraryTolerances = false
  BoxCorners = (2) [(-48.0834,-80.8335,-1e-07),(48.0834,80.8335,1e-07)]
  EqualTolerance = true
  ExtensionAngle = 0
  FormatSpec = %.2w
  FormatSpecOverTolerance = %+.2w
  FormatSpecUnderTolerance = %+.2w
  Inverted = false
  LineAngle = 0
  LockPosition = false
  MeasureType = 1
  OverTolerance = 0
  References2D = -> [View002]
  Rotation = 0
  Scale = 0.2
  ScaleType = 2
  TheoreticalExact = false
  Type = 2
  UnderTolerance = 0
  X = -78.5928
  Y = 52.695
FEATURE [TechDraw::DrawViewDimension] Dimension029  label="寸法029"
  AngleOverride = false
  Arbitrary = false
  ArbitraryTolerances = false
  BoxCorners = (2) [(-48.0834,-80.8335,-1e-07),(48.0834,80.8335,1e-07)]
  EqualTolerance = true
  ExtensionAngle = 0
  FormatSpec = %.2w
  FormatSpecOverTolerance = %+.2w
  FormatSpecUnderTolerance = %+.2w
  Inverted = false
  LineAngle = 0
  LockPosition = false
  MeasureType = 1
  OverTolerance = 0
  References2D = -> [View002]
  Rotation = 0
  Scale = 0.2
  ScaleType = 2
  TheoreticalExact = false
  Type = 2
  UnderTolerance = 0
  X = -78.5928
  Y = 1.03446
FEATURE [TechDraw::DrawPage] Page001  label="用紙001"
  KeepUpdated = true
  NextBalloonIndex = 1
  ProjectionType = 0
  Template = -> Template001
  Views = -> [View002,Dimension017,Dimension019,Dimension021,Dimension022,Dimension025,Dimension026,Dimension027,Dimension028,Dimension029]
